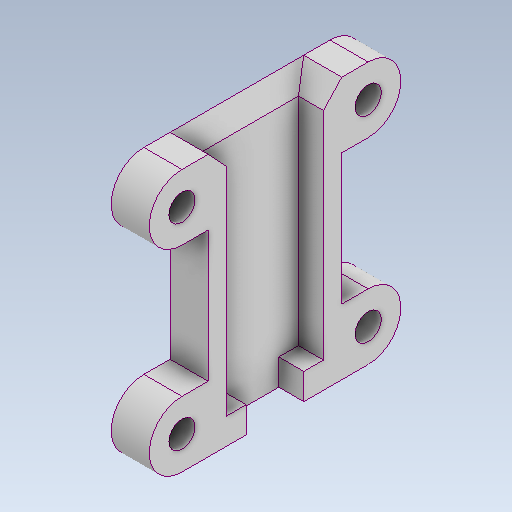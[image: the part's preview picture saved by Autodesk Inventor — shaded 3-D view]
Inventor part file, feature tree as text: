
AUTODESK INVENTOR PART (.ipt)
format: ipt  version: 2020 (Build 240168000, 168)  size: 171,008 bytes
history: native  units: in
note: dims shown in document units (in); Inventor stores cm internally (conversion verified against a paired STEP export)
features: other x3, sketch x3
ambient origin geometry x8: Origin, YZ Plane, XZ Plane, XY Plane, X Axis, Y Axis, Z Axis, Center Point
bodies: Solid1 (feature_tree)
feature tree (6):
  other  "PistonCasingBot.ipt"
  other  "Solid1::PistonCasingBot.ipt"
  other  "TaggingFeature1"
  sketch  "Sketch1"  dims[d0=0.3937in]
  sketch  "Sketch2"
  sketch  "Sketch3"
